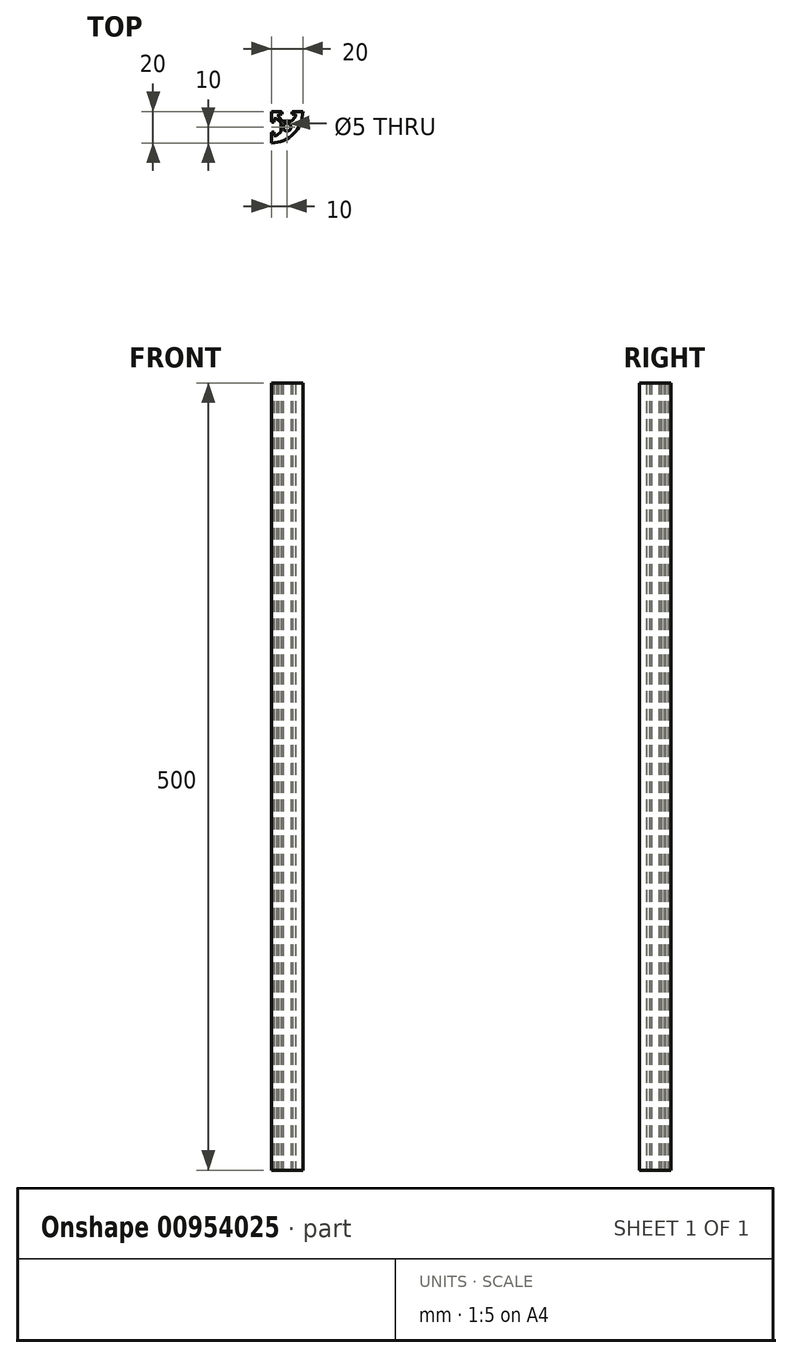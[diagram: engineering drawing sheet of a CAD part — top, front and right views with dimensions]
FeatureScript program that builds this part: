
annotation { "Feature Type Name" : "Feature", "Feature Type Description" : "" }
export const myFeature = defineFeature(function(context is Context, id is Id, definition is map)
    precondition{}
    {
        {
            var Q0;
            Q0=qCreatedBy(makeId("Top.planeOp"),FACE);
            var sketch = newSketch(context, id + "F0", { "sketchPlane" : qUnion([Q0])});
            skLineSegment(sketch, "E0", {"start": v(0, 0) * mm, "end": v(0, 6.4) * mm});
            skLineSegment(sketch, "E1", {"start": v(1.8, 6.9) * mm, "end": v(1.8, 4.5) * mm});
            skLineSegment(sketch, "E2", {"start": v(1.8, 4.5) * mm, "end": v(3.4, 4.5) * mm});
            skLineSegment(sketch, "E3", {"start": v(3.4, 4.5) * mm, "end": v(6.1, 7.2) * mm});
            skLineSegment(sketch, "E4", {"start": v(6.1, 7.2) * mm, "end": v(6.1, 10) * mm});
            skLineSegment(sketch, "E5", {"start": v(6.1, 10) * mm, "end": v(0, 10) * mm, "construction": true});
            skLineSegment(sketch, "E6", {"start": v(0, 6.4) * mm, "end": v(0.5, 6.4) * mm});
            skLineSegment(sketch, "E7", {"start": v(0.5, 6.4) * mm, "end": v(0.5, 6.9) * mm});
            skLineSegment(sketch, "E8", {"start": v(0.5, 6.9) * mm, "end": v(1.8, 6.9) * mm});
            skLineSegment(sketch, "E9.MirrorCS", {"start": v(0, 13.6) * mm, "end": v(0.5, 13.6) * mm});
            skLineSegment(sketch, "E10.MirrorCS", {"start": v(3.4, 15.5) * mm, "end": v(6.1, 12.8) * mm});
            skLineSegment(sketch, "E11.MirrorCS", {"start": v(1.8, 13.1) * mm, "end": v(1.8, 15.5) * mm});
            skLineSegment(sketch, "E12.MirrorCS", {"start": v(0.5, 13.6) * mm, "end": v(0.5, 13.1) * mm});
            skLineSegment(sketch, "E13.MirrorCS", {"start": v(1.8, 15.5) * mm, "end": v(3.4, 15.5) * mm});
            skLineSegment(sketch, "E14.MirrorCS", {"start": v(0.5, 13.1) * mm, "end": v(1.8, 13.1) * mm});
            skLineSegment(sketch, "E15.MirrorCS", {"start": v(6.1, 12.8) * mm, "end": v(6.1, 10) * mm});
            skLineSegment(sketch, "E16.MirrorCS", {"start": v(0, 20) * mm, "end": v(0, 13.6) * mm});
            skLineSegment(sketch, "E17", {"start": v(0, 20) * mm, "end": v(8.36, 11.64) * mm, "construction": true});
            skLineSegment(sketch, "E18.MirrorCS", {"start": v(13.6, 19.5) * mm, "end": v(13.1, 19.5) * mm});
            skLineSegment(sketch, "E19.MirrorCS", {"start": v(6.4, 19.5) * mm, "end": v(6.9, 19.5) * mm});
            skLineSegment(sketch, "E20.MirrorCS", {"start": v(6.4, 20) * mm, "end": v(6.4, 19.5) * mm});
            skLineSegment(sketch, "E21.MirrorCS", {"start": v(13.6, 20) * mm, "end": v(13.6, 19.5) * mm});
            skLineSegment(sketch, "E22.MirrorCS", {"start": v(15.5, 18.2) * mm, "end": v(15.5, 16.6) * mm});
            skLineSegment(sketch, "E23.MirrorCS", {"start": v(4.5, 18.2) * mm, "end": v(4.5, 16.6) * mm});
            skLineSegment(sketch, "E24.MirrorCS", {"start": v(13.1, 18.2) * mm, "end": v(15.5, 18.2) * mm});
            skLineSegment(sketch, "E25.MirrorCS", {"start": v(13.1, 19.5) * mm, "end": v(13.1, 18.2) * mm});
            skLineSegment(sketch, "E26.MirrorCS", {"start": v(12.8, 13.9) * mm, "end": v(10, 13.9) * mm});
            skLineSegment(sketch, "E27.MirrorCS", {"start": v(15.5, 16.6) * mm, "end": v(12.8, 13.9) * mm});
            skLineSegment(sketch, "E28.MirrorCS", {"start": v(7.2, 13.9) * mm, "end": v(10, 13.9) * mm});
            skLineSegment(sketch, "E29.MirrorCS", {"start": v(20, 20) * mm, "end": v(13.6, 20) * mm});
            skLineSegment(sketch, "E30.MirrorCS", {"start": v(6.9, 19.5) * mm, "end": v(6.9, 18.2) * mm});
            skLineSegment(sketch, "E31.MirrorCS", {"start": v(6.9, 18.2) * mm, "end": v(4.5, 18.2) * mm});
            skLineSegment(sketch, "E32.MirrorCS", {"start": v(4.5, 16.6) * mm, "end": v(7.2, 13.9) * mm});
            skLineSegment(sketch, "E33.MirrorCS", {"start": v(0, 20) * mm, "end": v(6.4, 20) * mm});
            skArc(sketch, "E34", {"start": v(0, 0) * mm, "mid": v(14.14, 5.86) * mm, "end": v(20, 20) * mm});
            skCircle(sketch, "E35", {"center": v(10, 10) * mm, "radius": 2.5 * mm});
            skSolve(sketch);
        }
        {
            var Q0;
            Q0 = qSketchRegion(id + "F0", true);
            extrude(context, id + "F1", {"entities" : qUnion([Q0]), "depth" : 500 * mm, "offsetDistance" : 25 * mm});
        }
    });
